# Revit family: P300240-060-CS
name_source: partatom
category: Lighting Fixtures
revit_build: Autodesk Revit 2014 (Build: 20130308_1515(x64)
units: mm (PartAtom-declared; Revit-internal decimal feet)

## types (1)
- P300240-060-CS
    Apparent Load = 34 VA
    Assembly Code = D5020200
    Color Filter = 16777215
    Connector Description = Lighting Connector
    Default Elevation = 48"
    Depth = 4 5/8"
    Description = This linear LED light fixture features a crisp opal white shade shaped into a tubular design with a seamless aesthetic. The fixture includes a 32w integrated LED bulb. This color temperature is color selectable for 3000K, 4000K or 5000K.
    Dimming Lamp Color Temperature Shift = <None>
    Emit Shape Visible in Rendering = No
    Emit from Rectangle Length = 35"
    Emit from Rectangle Width = 2"
    Fixture distribution = Direct
    Glass = Hubbell - Glass
    Gold = Hubbell - Gold
    Height = 5 5/8"
    Housing Material = Hubbell - White Glass
    Lamp = LED
    Load Classification = Lighting
    Manufacturer = Progress Lighting
    Model = P300240-060-CS
    Photometric Web File = generic
    Power Factor = 1
    Product Documentation Link = https://hubbellcdn.com
    Product Link = https://www.hubbell.com
    Specifications = Features a crisp opal white shade shaped into a tubular design with a seamless aesthetic.
CCT selectable (3000K, 4000K, 5000K). Internal switch allows color selection.
90 CRI.
2760 delivered lumens.
Perfect for any modern, luxury, or transitional settings.
Measures 38-1/4-inch width by 6-1/8-inch height.
Uses one integrated LED that is included (30w max).
Includes installation instructions and mounting hardware.
Progress Lighting products are designed for exceptional quality, reliability, and functionality.
    Tilt Angle = 60.00°
    URL = https://www.hubbell.com
    Voltage = 120 V
    Warranty = 5 years Warranty
    Wattage Comments = 34W
    Watts = 34 W
    White = Paint - Hubbell - Matte White
    Width = 37 3/4"

## geometry (parser evidence)
native form markers: Sweep x5
no freeform markers — native parametric forms only
